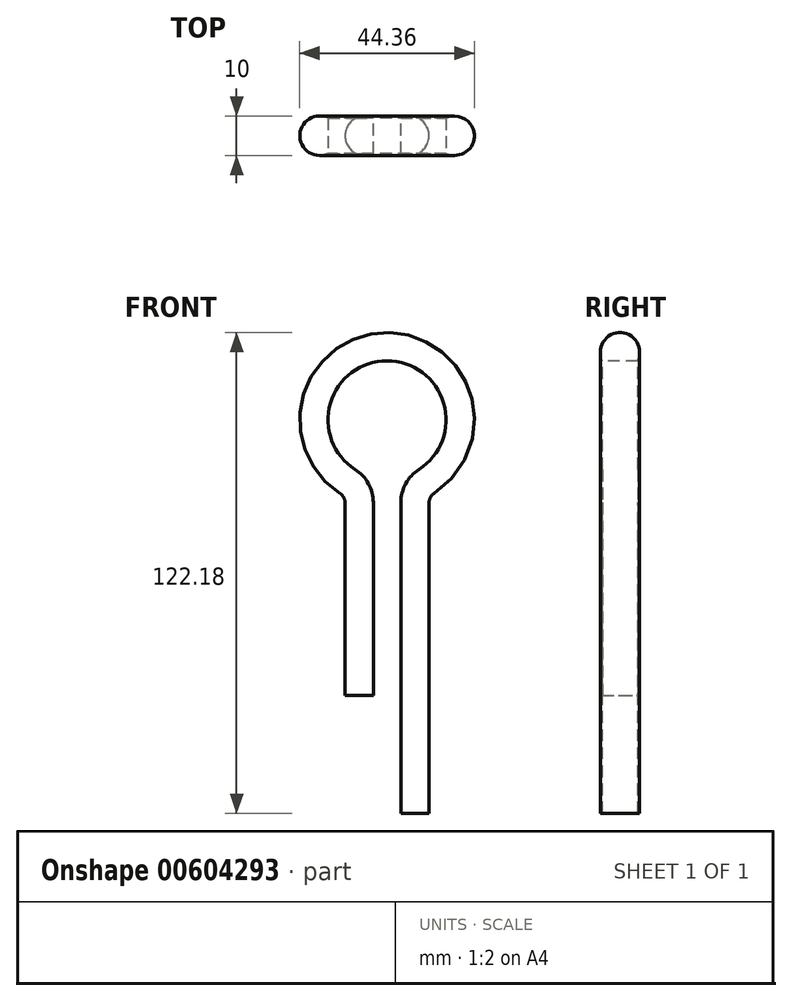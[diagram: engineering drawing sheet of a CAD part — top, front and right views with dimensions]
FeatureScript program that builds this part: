
annotation { "Feature Type Name" : "Feature", "Feature Type Description" : "" }
export const myFeature = defineFeature(function(context is Context, id is Id, definition is map)
    precondition{}
    {
        {
            var Q0;
            Q0=qCreatedBy(makeId("Top.planeOp"),FACE);
            var sketch = newSketch(context, id + "F0", { "sketchPlane" : qUnion([Q0])});
            skLineSegment(sketch, "E0", {"start": v(3.5, -4.5) * mm, "end": v(3.5, 4.5) * mm});
            skArc(sketch, "E1", {"start": v(3.5, -4.5) * mm, "mid": v(10.68, 0) * mm, "end": v(3.5, 4.5) * mm});
            skSolve(sketch);
        }
        {
            var Q0;
            Q0=qCreatedBy(makeId("Front.planeOp"),FACE);
            var sketch = newSketch(context, id + "F1", { "sketchPlane" : qUnion([Q0])});
            skLineSegment(sketch, "E2", {"start": v(3.5, -67.77) * mm, "end": v(3.5, 11.2) * mm});
            skLineSegment(sketch, "E3", {"start": v(-3.5, 11.2) * mm, "end": v(-3.5, -37.77) * mm});
            skArc(sketch, "E4", {"start": v(8.1, 19.6) * mm, "mid": v(0, 47.23) * mm, "end": v(-8.1, 19.6) * mm});
            skPoint(sketch, "E5.visualSharp", {"position": v(-3.5, 17.65) * mm});
            skArc(sketch, "E5.filletArc", {"start": v(-3.5, 11.2) * mm, "mid": v(-4.73, 15.99) * mm, "end": v(-8.1, 19.6) * mm});
            skPoint(sketch, "E6.visualSharp", {"position": v(3.5, 17.65) * mm});
            skArc(sketch, "E6.filletArc", {"start": v(8.1, 19.6) * mm, "mid": v(4.73, 15.99) * mm, "end": v(3.5, 11.2) * mm});
            skSolve(sketch);
        }
        {
            var Q0;
            Q0=makeQuery(id+"F0.imprint","IMPRINT",FACE,{"disambiguationData":[TD([[makeQuery(id+"F0.imprint","IMPRINT",EDGE,{"derivedFrom":sQuery(id+"F0.wireOp",EDGE,"E0")}),-1.0]])]});
            var Q1;
            Q1 = qConstructionFilter(qBodyType(qCreatedBy(id + "F1" ,EDGE), BodyType.WIRE), ConstructionObject.NO);
            sweep(context, id + "F2", {"profiles" : qUnion([Q0]), "path" : qUnion([Q1])});
        }
    });
